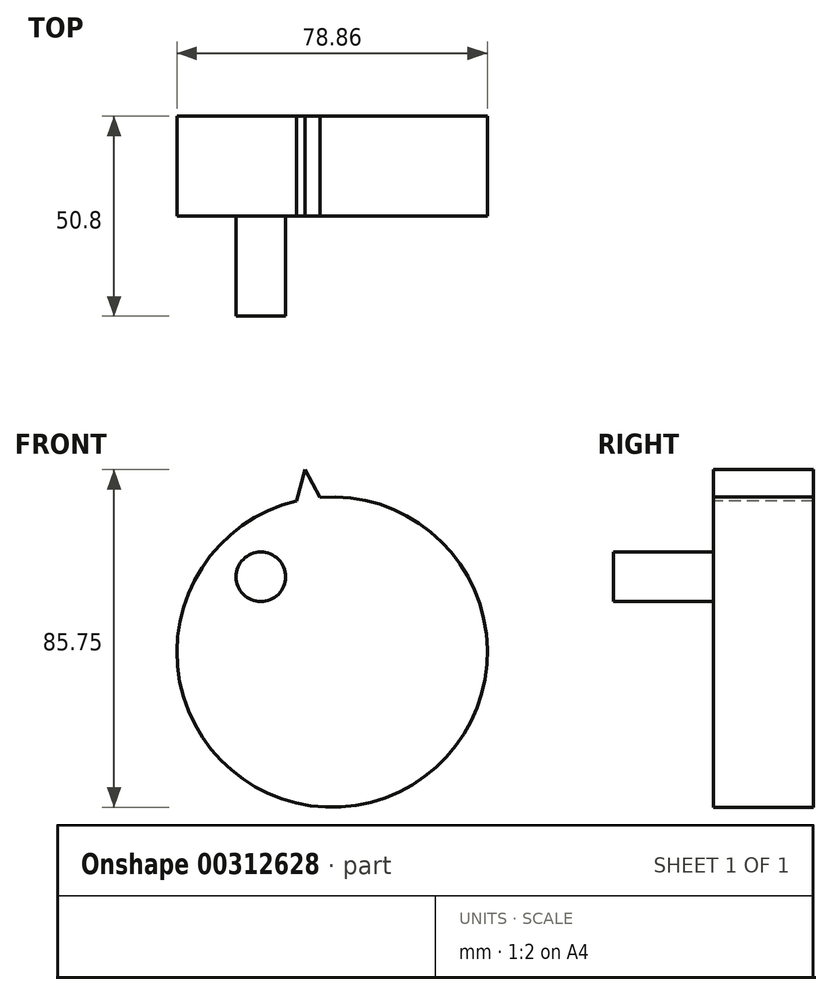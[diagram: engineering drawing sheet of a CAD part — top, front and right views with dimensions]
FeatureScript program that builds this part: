
annotation { "Feature Type Name" : "Feature", "Feature Type Description" : "" }
export const myFeature = defineFeature(function(context is Context, id is Id, definition is map)
    precondition{}
    {
        {
            var Q0;
            Q0=qCreatedBy(makeId("Front.planeOp"),FACE);
            var sketch = newSketch(context, id + "F0", { "sketchPlane" : qUnion([Q0])});
            skCircle(sketch, "E0", {"center": v(0, 0) * mm, "radius": 39.43 * mm});
            skSolve(sketch);
        }
        {
            var Q0;
            Q0 = qSketchRegion(id + "F0", true);
            extrude(context, id + "F1", {"entities" : qUnion([Q0]), "depth" : 25.4 * mm});
        }
        {
            var Q0;
            Q0=makeQuery(id+"F1.opExtrude","CAP_FACE",FACE,{"disambiguationData":[OSD([sQuery(id+"F0.wireOp",EDGE,"E0")])],"isStart":false});
            var sketch = newSketch(context, id + "F2", { "sketchPlane" : qUnion([Q0])});
            skCircle(sketch, "E1", {"center": v(-18.13, 19.12) * mm, "radius": 6.29 * mm});
            skSolve(sketch);
        }
        {
            var Q0;
            Q0 = qSketchRegion(id + "F2", true);
            extrude(context, id + "F3", {"entities" : qUnion([Q0]), "operationType" : NewBodyOperationType.ADD, "depth" : 25.4 * mm});
        }
        {
            var Q0;
            {var subQ0=sQuery(id+"F2.wireOp",EDGE,"E1");var subQ1=sQuery(id+"F0.wireOp",EDGE,"E0");Q0=makeQuery(id+"FsIcr5FVyK4INmj_1.28.F3.boolean.opBoolean","SPLIT",FACE,{"disambiguationData":[TD([makeQuery(id+"F1.opExtrude","SWEPT_FACE",FACE,{"disambiguationData":[OSD([subQ1])]}),makeQuery(id+"F3.opExtrude","SWEPT_FACE",FACE,{"disambiguationData":[OSD([subQ0])]}),makeQuery(id+"FsIcr5FVyK4INmj_1.1.F3.opExtrude","SWEPT_FACE",FACE,{"disambiguationData":[OSD([subQ0])]}),makeQuery(id+"FsIcr5FVyK4INmj_1.2.F3.opExtrude","SWEPT_FACE",FACE,{"disambiguationData":[OSD([subQ0])]}),makeQuery(id+"FsIcr5FVyK4INmj_1.3.F3.opExtrude","SWEPT_FACE",FACE,{"disambiguationData":[OSD([subQ0])]}),makeQuery(id+"FsIcr5FVyK4INmj_1.4.F3.opExtrude","SWEPT_FACE",FACE,{"disambiguationData":[OSD([subQ0])]}),makeQuery(id+"FsIcr5FVyK4INmj_1.5.F3.opExtrude","SWEPT_FACE",FACE,{"disambiguationData":[OSD([subQ0])]}),makeQuery(id+"FsIcr5FVyK4INmj_1.6.F3.opExtrude","SWEPT_FACE",FACE,{"disambiguationData":[OSD([subQ0])]}),makeQuery(id+"FsIcr5FVyK4INmj_1.7.F3.opExtrude","SWEPT_FACE",FACE,{"disambiguationData":[OSD([subQ0])]}),makeQuery(id+"FsIcr5FVyK4INmj_1.8.F3.opExtrude","SWEPT_FACE",FACE,{"disambiguationData":[OSD([subQ0])]}),makeQuery(id+"FsIcr5FVyK4INmj_1.9.F3.opExtrude","SWEPT_FACE",FACE,{"disambiguationData":[OSD([subQ0])]}),makeQuery(id+"FsIcr5FVyK4INmj_1.10.F3.opExtrude","SWEPT_FACE",FACE,{"disambiguationData":[OSD([subQ0])]}),makeQuery(id+"FsIcr5FVyK4INmj_1.11.F3.opExtrude","SWEPT_FACE",FACE,{"disambiguationData":[OSD([subQ0])]}),makeQuery(id+"FsIcr5FVyK4INmj_1.12.F3.opExtrude","SWEPT_FACE",FACE,{"disambiguationData":[OSD([subQ0])]}),makeQuery(id+"FsIcr5FVyK4INmj_1.13.F3.opExtrude","SWEPT_FACE",FACE,{"disambiguationData":[OSD([subQ0])]}),makeQuery(id+"FsIcr5FVyK4INmj_1.14.F3.opExtrude","SWEPT_FACE",FACE,{"disambiguationData":[OSD([subQ0])]}),makeQuery(id+"FsIcr5FVyK4INmj_1.15.F3.opExtrude","SWEPT_FACE",FACE,{"disambiguationData":[OSD([subQ0])]}),makeQuery(id+"FsIcr5FVyK4INmj_1.16.F3.opExtrude","SWEPT_FACE",FACE,{"disambiguationData":[OSD([subQ0])]}),makeQuery(id+"FsIcr5FVyK4INmj_1.17.F3.opExtrude","SWEPT_FACE",FACE,{"disambiguationData":[OSD([subQ0])]}),makeQuery(id+"FsIcr5FVyK4INmj_1.18.F3.opExtrude","SWEPT_FACE",FACE,{"disambiguationData":[OSD([subQ0])]}),makeQuery(id+"FsIcr5FVyK4INmj_1.19.F3.opExtrude","SWEPT_FACE",FACE,{"disambiguationData":[OSD([subQ0])]}),makeQuery(id+"FsIcr5FVyK4INmj_1.20.F3.opExtrude","SWEPT_FACE",FACE,{"disambiguationData":[OSD([subQ0])]}),makeQuery(id+"FsIcr5FVyK4INmj_1.21.F3.opExtrude","SWEPT_FACE",FACE,{"disambiguationData":[OSD([subQ0])]}),makeQuery(id+"FsIcr5FVyK4INmj_1.22.F3.opExtrude","SWEPT_FACE",FACE,{"disambiguationData":[OSD([subQ0])]}),makeQuery(id+"FsIcr5FVyK4INmj_1.23.F3.opExtrude","SWEPT_FACE",FACE,{"disambiguationData":[OSD([subQ0])]}),makeQuery(id+"FsIcr5FVyK4INmj_1.24.F3.opExtrude","SWEPT_FACE",FACE,{"disambiguationData":[OSD([subQ0])]}),makeQuery(id+"FsIcr5FVyK4INmj_1.25.F3.opExtrude","SWEPT_FACE",FACE,{"disambiguationData":[OSD([subQ0])]}),makeQuery(id+"FsIcr5FVyK4INmj_1.26.F3.opExtrude","SWEPT_FACE",FACE,{"disambiguationData":[OSD([subQ0])]}),makeQuery(id+"FsIcr5FVyK4INmj_1.27.F3.opExtrude","SWEPT_FACE",FACE,{"disambiguationData":[OSD([subQ0])]}),makeQuery(id+"FsIcr5FVyK4INmj_1.28.F3.opExtrude","SWEPT_FACE",FACE,{"disambiguationData":[OSD([subQ0])]})])],"derivedFrom":makeQuery(id+"F1.opExtrude","CAP_FACE",FACE,{"disambiguationData":[OSD([subQ1])],"isStart":false})});}
            var sketch = newSketch(context, id + "F4", { "sketchPlane" : qUnion([Q0])});
            skLineSegment(sketch, "E2", {"start": v(-9, 38.4) * mm, "end": v(-6.92, 46.32) * mm});
            skLineSegment(sketch, "E3", {"start": v(-6.92, 46.32) * mm, "end": v(-3.12, 39.31) * mm});
            skLineSegment(sketch, "E4", {"start": v(-3.12, 39.31) * mm, "end": v(-9, 38.4) * mm});
            skSolve(sketch);
        }
        {
            var Q0;
            Q0 = qSketchRegion(id + "F4", true);
            extrude(context, id + "F5", {"entities" : qUnion([Q0]), "operationType" : NewBodyOperationType.ADD, "oppositeDirection" : true, "depth" : 25.4 * mm});
        }
    });
